FCSTD DOCUMENT  (FreeCAD 0.19R18750 (Git))
Label: #110-000 Assembly3
License: All rights reserved
LicenseURL: http://en.wikipedia.org/wiki/All_rights_reserved
objects: App::Link×90, Part::Feature×15, App::LinkGroup×1
note: 15 computed .brp shape members not serialized (recipe doc carries the construction recipe); baked Part::Feature solids carry a one-line shape summary decoded from their .brp

FEATURE [Part::Feature] Solid  label="XR5_R_CC25_P10.16_H_5DD3C33E"
  Placement = pos=(35.2425,24.765,0) rot=(0,0,1;1.5708rad)
  shape: bbox 2.5 x 10.96 x 5.1 mm, 11 faces (baked)
FEATURE [App::Link] Link  label="XR5_R_CC25_P10.16_H_5DD3C33E001"
  LinkPlacement = pos=(10.4775,-2.54,0) rot=(0,0,1;1.5708rad)
  LinkedObject = -> Solid
  Placement = pos=(10.4775,-2.54,0) rot=(0,0,1;1.5708rad)
FEATURE [Part::Feature] Solid001  label="RV55_Alpha_RV16AF-41-15R-XXX_5DD3C757"
  Placement = pos=(0,58.42,0) rot=(0,0,1;1.5708rad)
  shape: bbox 24.75 x 17.02 x 30.75 mm, 459 faces (baked)
FEATURE [App::Link] Link001  label="RV55_Alpha_RV16AF-41-15R-XXX_5DD3C758"
  LinkPlacement = pos=(-43.4975,58.42,0) rot=(0,0,1;1.5708rad)
  LinkedObject = -> Solid001
  Placement = pos=(-43.4975,58.42,0) rot=(0,0,1;1.5708rad)
FEATURE [Part::Feature] Solid002  label="JP20_R_0R_Wire_Jumper_P10.16_5DC277DA"
  Placement = pos=(13.6525,15.24,0) rot=(0,0,1;3.14159rad)
  shape: bbox 10.88 x 0.55 x 3.709 mm, 7 faces (baked)
FEATURE [App::Link] Link002  label="JP20_R_0R_Wire_Jumper_P10.16_5DC277DA001"
  LinkPlacement = pos=(13.6525,22.86,0) rot=(0,0,1;0rad)
  LinkedObject = -> Solid002
  Placement = pos=(13.6525,22.86,0) rot=(0,0,1;0rad)
FEATURE [App::Link] Link003  label="JP20_R_0R_Wire_Jumper_P10.16_5DC277DA002"
  LinkPlacement = pos=(10.4775,82.55,0) rot=(0,0,1;0rad)
  LinkedObject = -> Solid002
  Placement = pos=(10.4775,82.55,0) rot=(0,0,1;0rad)
FEATURE [App::Link] Link004  label="JP20_R_0R_Wire_Jumper_P10.16_5DC277DA003"
  LinkPlacement = pos=(26.9875,19.05,0) rot=(0,0,1;1.5708rad)
  LinkedObject = -> Solid002
  Placement = pos=(26.9875,19.05,0) rot=(0,0,1;1.5708rad)
FEATURE [App::Link] Link005  label="JP20_R_0R_Wire_Jumper_P10.16_5DC277DA004"
  LinkPlacement = pos=(27.6225,50.165,0) rot=(0,0,1;3.14159rad)
  LinkedObject = -> Solid002
  Placement = pos=(27.6225,50.165,0) rot=(0,0,1;3.14159rad)
FEATURE [App::Link] Link006  label="JP20_R_0R_Wire_Jumper_P10.16_5DC277DA005"
  LinkPlacement = pos=(13.0175,50.165,0) rot=(0,0,1;3.14159rad)
  LinkedObject = -> Solid002
  Placement = pos=(13.0175,50.165,0) rot=(0,0,1;3.14159rad)
FEATURE [App::Link] Link007  label="JP20_R_0R_Wire_Jumper_P10.16_5DC277DA006"
  LinkPlacement = pos=(30.1625,29.21,0) rot=(0,0,1;1.5708rad)
  LinkedObject = -> Solid002
  Placement = pos=(30.1625,29.21,0) rot=(0,0,1;1.5708rad)
FEATURE [App::Link] Link008  label="JP20_R_0R_Wire_Jumper_P10.16_5DC277DA007"
  LinkPlacement = pos=(13.6525,19.05,0) rot=(0,0,1;3.14159rad)
  LinkedObject = -> Solid002
  Placement = pos=(13.6525,19.05,0) rot=(0,0,1;3.14159rad)
FEATURE [App::Link] Link009  label="JP20_R_0R_Wire_Jumper_P10.16_5DC277DA008"
  LinkPlacement = pos=(-2.2225,12.065,0) rot=(0,0,-1;1.5708rad)
  LinkedObject = -> Solid002
  Placement = pos=(-2.2225,12.065,0) rot=(0,0,-1;1.5708rad)
FEATURE [App::Link] Link010  label="JP20_R_0R_Wire_Jumper_P10.16_5DC277DA009"
  LinkPlacement = pos=(-14.2875,31.75,0) rot=(0,0,1;3.14159rad)
  LinkedObject = -> Solid002
  Placement = pos=(-14.2875,31.75,0) rot=(0,0,1;3.14159rad)
FEATURE [App::Link] Link011  label="JP20_R_0R_Wire_Jumper_P10.16_5DC277DA010"
  LinkPlacement = pos=(-24.4475,10.16,0) rot=(0,0,1;1.5708rad)
  LinkedObject = -> Solid002
  Placement = pos=(-24.4475,10.16,0) rot=(0,0,1;1.5708rad)
FEATURE [App::Link] Link012  label="JP20_R_0R_Wire_Jumper_P10.16_5DC277DA011"
  LinkPlacement = pos=(-34.6075,21.59,0) rot=(0,0,1;1.5708rad)
  LinkedObject = -> Solid002
  Placement = pos=(-34.6075,21.59,0) rot=(0,0,1;1.5708rad)
FEATURE [App::Link] Link013  label="JP20_R_0R_Wire_Jumper_P10.16_5DC277DA012"
  LinkPlacement = pos=(26.9875,66.675,0) rot=(0,0,1;0rad)
  LinkedObject = -> Solid002
  Placement = pos=(26.9875,66.675,0) rot=(0,0,1;0rad)
FEATURE [App::Link] Link014  label="JP20_R_0R_Wire_Jumper_P10.16_5DC277DA013"
  LinkPlacement = pos=(-11.7475,67.31,0) rot=(0,0,1;0rad)
  LinkedObject = -> Solid002
  Placement = pos=(-11.7475,67.31,0) rot=(0,0,1;0rad)
FEATURE [App::Link] Link015  label="JP20_R_0R_Wire_Jumper_P10.16_5DC277DA014"
  LinkPlacement = pos=(-17.4625,81.915,0) rot=(0,0,1;0rad)
  LinkedObject = -> Solid002
  Placement = pos=(-17.4625,81.915,0) rot=(0,0,1;0rad)
FEATURE [Part::Feature] Solid003  label="XC7_Nichicon_UMA_Straight_D8_H5_P2.5_d0.45_LL2.6_5DC00BE9"
  Placement = pos=(11.7475,7.62,0) rot=(0,0,1;1.5708rad)
  shape: bbox 8.659 x 8.659 x 7.61 mm, 57 faces (baked)
FEATURE [Part::Feature] Solid004  label="RV52_User_Library_3362P_2_sp_5D8A0BC8"
  Placement = pos=(18.0975,74.93,0) rot=(0,0,1;0rad)
  shape: bbox 6.706 x 7.036 x 10.16 mm, 550 faces (baked)
FEATURE [Part::Feature] Solid005  label="XC8_FKS2G021001C00KSSD_5DC00BFC"
  Placement = pos=(2.2225,-2.5,0) rot=(0,0,-1;1.5708rad)
  shape: bbox 4.65 x 15.3 x 10.5 mm, 403 faces (baked)
FEATURE [Part::Feature] Solid006  label="XC6_Capacitor_Electrolytic_THT_Radial_Angled_D10_H17_P5_d0.6_h1.5_LL2.6_5DC00BE2"
  Placement = pos=(21.9075,-8.89,0) rot=(0,0,1;0rad)
  shape: bbox 10.82 x 18.92 x 13.01 mm, 66 faces (baked)
FEATURE [Part::Feature] Solid007  label="XC12_Nichicon_UMA_Straight_D8_H5_P2.5_d0.45_LL2.6_5DCF4B87"
  Placement = pos=(48.5775,22.86,0) rot=(0,0,-1;1.5708rad)
  shape: bbox 8.659 x 8.659 x 7.61 mm, 57 faces (baked)
FEATURE [Part::Feature] Solid008  label="XC10_Nichicon_UMA_Straight_D5_H5_P2_d0.45_LL2.6_5DC00C0A"
  Placement = pos=(44.1325,1.905,0) rot=(0,0,1;0rad)
  shape: bbox 5.412 x 5.412 x 7.61 mm, 57 faces (baked)
FEATURE [App::Link] Link016  label="XC10_Nichicon_UMA_Straight_D5_H5_P2_d0.45_LL2.6_5DC00C0A001"
  LinkPlacement = pos=(39.6875,-1.905,0) rot=(0,0,1;0rad)
  LinkedObject = -> Solid008
  Placement = pos=(39.6875,-1.905,0) rot=(0,0,1;0rad)
FEATURE [App::Link] Link017  label="XC12_Nichicon_UMA_Straight_D8_H5_P2.5_d0.45_LL2.6_5DCF4B088"
  LinkPlacement = pos=(44.7675,-6.985,0) rot=(0,0,1;0rad)
  LinkedObject = -> Solid007
  Placement = pos=(44.7675,-6.985,0) rot=(0,0,1;0rad)
FEATURE [App::Link] Link018  label="XC10_Nichicon_UMA_Straight_D5_H5_P2_d0.45_LL2.6_5DC00C0A002"
  LinkPlacement = pos=(-46.6725,5.715,0) rot=(0,0,-1;1.5708rad)
  LinkedObject = -> Solid008
  Placement = pos=(-46.6725,5.715,0) rot=(0,0,-1;1.5708rad)
FEATURE [Part::Feature] Solid009  label="XD6_DO-41_P10.16_5DC00C72"
  Placement = pos=(13.0175,-2.54,0) rot=(0,0,1;1.5708rad)
  shape: bbox 2.395 x 11.21 x 4.985 mm, 15 faces (baked)
FEATURE [App::Link] Link019  label="XD6_DO-41_P10.16_5DC00C073"
  LinkPlacement = pos=(-39.6875,-2.54,0) rot=(0,0,1;1.5708rad)
  LinkedObject = -> Solid009
  Placement = pos=(-39.6875,-2.54,0) rot=(0,0,1;1.5708rad)
FEATURE [App::Link] Link020  label="XD6_DO-41_P10.16_5DC00C074"
  LinkPlacement = pos=(42.2275,72.39,0) rot=(0,0,1;1.5708rad)
  LinkedObject = -> Solid009
  Placement = pos=(42.2275,72.39,0) rot=(0,0,1;1.5708rad)
FEATURE [App::Link] Link021  label="XR5_R_CC25_P10.16_H_5DD3C33E002"
  LinkPlacement = pos=(32.7025,29.21,0) rot=(0,0,1;1.5708rad)
  LinkedObject = -> Solid
  Placement = pos=(32.7025,29.21,0) rot=(0,0,1;1.5708rad)
FEATURE [App::Link] Link022  label="XR5_R_CC25_P10.16_H_5DD3C33E003"
  LinkPlacement = pos=(15.5575,-2.54,0) rot=(0,0,1;1.5708rad)
  LinkedObject = -> Solid
  Placement = pos=(15.5575,-2.54,0) rot=(0,0,1;1.5708rad)
FEATURE [App::Link] Link023  label="XR5_R_CC25_P10.16_H_5DD3C33E004"
  LinkPlacement = pos=(-42.2275,-2.54,0) rot=(0,0,-1;1.5708rad)
  LinkedObject = -> Solid
  Placement = pos=(-42.2275,-2.54,0) rot=(0,0,-1;1.5708rad)
FEATURE [App::Link] Link024  label="XR5_R_CC25_P10.16_H_5DD3C33E005"
  LinkPlacement = pos=(-51.1175,40.64,0) rot=(0,0,1;1.5708rad)
  LinkedObject = -> Solid
  Placement = pos=(-51.1175,40.64,0) rot=(0,0,1;1.5708rad)
FEATURE [App::Link] Link025  label="XR5_R_CC25_P10.16_H_5DD3C33E006"
  LinkPlacement = pos=(50.4825,74.93,0) rot=(0,0,1;1.5708rad)
  LinkedObject = -> Solid
  Placement = pos=(50.4825,74.93,0) rot=(0,0,1;1.5708rad)
FEATURE [App::Link] Link026  label="XR5_R_CC25_P10.16_H_5DD3C33E007"
  LinkPlacement = pos=(44.7675,78.74,0) rot=(0,0,-1;1.5708rad)
  LinkedObject = -> Solid
  Placement = pos=(44.7675,78.74,0) rot=(0,0,-1;1.5708rad)
FEATURE [App::Link] Link027  label="XR5_R_CC25_P10.16_H_5DD3C33E008"
  LinkPlacement = pos=(-20.6375,-2.54,0) rot=(0,0,-1;1.5708rad)
  LinkedObject = -> Solid
  Placement = pos=(-20.6375,-2.54,0) rot=(0,0,-1;1.5708rad)
FEATURE [App::Link] Link028  label="XR5_R_CC25_P10.16_H_5DD3C33E009"
  LinkPlacement = pos=(-37.1475,-2.54,0) rot=(0,0,-1;1.5708rad)
  LinkedObject = -> Solid
  Placement = pos=(-37.1475,-2.54,0) rot=(0,0,-1;1.5708rad)
FEATURE [App::Link] Link029  label="XR5_R_CC25_P10.16_H_5DD3C33E010"
  LinkPlacement = pos=(-23.1775,-2.54,0) rot=(0,0,-1;1.5708rad)
  LinkedObject = -> Solid
  Placement = pos=(-23.1775,-2.54,0) rot=(0,0,-1;1.5708rad)
FEATURE [App::Link] Link030  label="XR5_R_CC25_P10.16_H_5DD3C33E011"
  LinkPlacement = pos=(-34.6075,-2.54,0) rot=(0,0,-1;1.5708rad)
  LinkedObject = -> Solid
  Placement = pos=(-34.6075,-2.54,0) rot=(0,0,-1;1.5708rad)
FEATURE [App::Link] Link031  label="XR5_R_CC25_P10.16_H_5DD3C33E012"
  LinkPlacement = pos=(-29.5275,-2.54,0) rot=(0,0,-1;1.5708rad)
  LinkedObject = -> Solid
  Placement = pos=(-29.5275,-2.54,0) rot=(0,0,-1;1.5708rad)
FEATURE [App::Link] Link032  label="XR5_R_CC25_P10.16_H_5DD3C33E013"
  LinkPlacement = pos=(-7.9375,-2.54,0) rot=(0,0,-1;1.5708rad)
  LinkedObject = -> Solid
  Placement = pos=(-7.9375,-2.54,0) rot=(0,0,-1;1.5708rad)
FEATURE [App::Link] Link033  label="XR5_R_CC25_P10.16_H_5DD3C33E014"
  LinkPlacement = pos=(-5.3975,-2.54,0) rot=(0,0,-1;1.5708rad)
  LinkedObject = -> Solid
  Placement = pos=(-5.3975,-2.54,0) rot=(0,0,-1;1.5708rad)
FEATURE [App::Link] Link034  label="XR5_R_CC25_P10.16_H_5DD3C33E015"
  LinkPlacement = pos=(18.7325,58.42,0) rot=(0,0,-1;1.5708rad)
  LinkedObject = -> Solid
  Placement = pos=(18.7325,58.42,0) rot=(0,0,-1;1.5708rad)
FEATURE [App::Link] Link035  label="XR5_R_CC25_P10.16_H_5DD3C33E016"
  LinkPlacement = pos=(23.8125,58.42,0) rot=(0,0,-1;1.5708rad)
  LinkedObject = -> Solid
  Placement = pos=(23.8125,58.42,0) rot=(0,0,-1;1.5708rad)
FEATURE [App::Link] Link036  label="XR5_R_CC25_P10.16_H_5DD3C33E017"
  LinkPlacement = pos=(21.2725,58.42,0) rot=(0,0,-1;1.5708rad)
  LinkedObject = -> Solid
  Placement = pos=(21.2725,58.42,0) rot=(0,0,-1;1.5708rad)
FEATURE [App::Link] Link037  label="XR5_R_CC25_P10.16_H_5DD3C33E018"
  LinkPlacement = pos=(29.5275,74.93,0) rot=(0,0,1;1.5708rad)
  LinkedObject = -> Solid
  Placement = pos=(29.5275,74.93,0) rot=(0,0,1;1.5708rad)
FEATURE [App::Link] Link038  label="XR5_R_CC25_P10.16_H_5DD3C33E019"
  LinkPlacement = pos=(26.9875,74.93,0) rot=(0,0,-1;1.5708rad)
  LinkedObject = -> Solid
  Placement = pos=(26.9875,74.93,0) rot=(0,0,-1;1.5708rad)
FEATURE [App::Link] Link039  label="XR5_R_CC25_P10.16_H_5DD3C33E020"
  LinkPlacement = pos=(-44.7675,-2.54,0) rot=(0,0,-1;1.5708rad)
  LinkedObject = -> Solid
  Placement = pos=(-44.7675,-2.54,0) rot=(0,0,-1;1.5708rad)
FEATURE [App::Link] Link040  label="XR5_R_CC25_P10.16_H_5DD3C33E021"
  LinkPlacement = pos=(-37.7825,10.16,0) rot=(0,0,1;1.5708rad)
  LinkedObject = -> Solid
  Placement = pos=(-37.7825,10.16,0) rot=(0,0,1;1.5708rad)
FEATURE [App::Link] Link041  label="XR5_R_CC25_P10.16_H_5DD3C33E022"
  LinkPlacement = pos=(-47.9425,24.13,0) rot=(0,0,-1;1.5708rad)
  LinkedObject = -> Solid
  Placement = pos=(-47.9425,24.13,0) rot=(0,0,-1;1.5708rad)
FEATURE [App::Link] Link042  label="XR5_R_CC25_P10.16_H_5DD3C33E023"
  LinkPlacement = pos=(-50.4825,24.13,0) rot=(0,0,1;1.5708rad)
  LinkedObject = -> Solid
  Placement = pos=(-50.4825,24.13,0) rot=(0,0,1;1.5708rad)
FEATURE [App::Link] Link043  label="XR5_R_CC25_P10.16_H_5DD3C33E024"
  LinkPlacement = pos=(-44.1325,24.13,0) rot=(0,0,1;1.5708rad)
  LinkedObject = -> Solid
  Placement = pos=(-44.1325,24.13,0) rot=(0,0,1;1.5708rad)
FEATURE [App::Link] Link044  label="XR5_R_CC25_P10.16_H_5DD3C33E025"
  LinkPlacement = pos=(-40.3225,24.13,0) rot=(0,0,1;1.5708rad)
  LinkedObject = -> Solid
  Placement = pos=(-40.3225,24.13,0) rot=(0,0,1;1.5708rad)
FEATURE [App::Link] Link045  label="XR5_R_CC25_P10.16_H_5DD3C33E026"
  LinkPlacement = pos=(18.0975,40.64,0) rot=(0,0,-1;1.5708rad)
  LinkedObject = -> Solid
  Placement = pos=(18.0975,40.64,0) rot=(0,0,-1;1.5708rad)
FEATURE [App::Link] Link046  label="XR5_R_CC25_P10.16_H_5DD3C33E027"
  LinkPlacement = pos=(5.3975,74.93,0) rot=(0,0,1;1.5708rad)
  LinkedObject = -> Solid
  Placement = pos=(5.3975,74.93,0) rot=(0,0,1;1.5708rad)
FEATURE [App::Link] Link047  label="XR5_R_CC25_P10.16_H_5DD3C33E028"
  LinkPlacement = pos=(2.8575,74.93,0) rot=(0,0,-1;1.5708rad)
  LinkedObject = -> Solid
  Placement = pos=(2.8575,74.93,0) rot=(0,0,-1;1.5708rad)
FEATURE [App::Link] Link048  label="XR5_R_CC25_P10.16_H_5DD3C33E029"
  LinkPlacement = pos=(15.5575,40.64,0) rot=(0,0,-1;1.5708rad)
  LinkedObject = -> Solid
  Placement = pos=(15.5575,40.64,0) rot=(0,0,-1;1.5708rad)
FEATURE [App::Link] Link049  label="XR5_R_CC25_P10.16_H_5DD3C33E030"
  LinkPlacement = pos=(-0.9525,74.93,0) rot=(0,0,-1;1.5708rad)
  LinkedObject = -> Solid
  Placement = pos=(-0.9525,74.93,0) rot=(0,0,-1;1.5708rad)
FEATURE [App::Link] Link050  label="XR5_R_CC25_P10.16_H_5DD3C33E031"
  LinkPlacement = pos=(8.5725,40.64,0) rot=(0,0,-1;1.5708rad)
  LinkedObject = -> Solid
  Placement = pos=(8.5725,40.64,0) rot=(0,0,-1;1.5708rad)
FEATURE [App::Link] Link051  label="XR5_R_CC25_P10.16_H_5DD3C33E032"
  LinkPlacement = pos=(6.0325,40.64,0) rot=(0,0,1;1.5708rad)
  LinkedObject = -> Solid
  Placement = pos=(6.0325,40.64,0) rot=(0,0,1;1.5708rad)
FEATURE [App::Link] Link052  label="XR5_R_CC25_P10.16_H_5DD3C33E033"
  LinkPlacement = pos=(-1.5875,40.64,0) rot=(0,0,-1;1.5708rad)
  LinkedObject = -> Solid
  Placement = pos=(-1.5875,40.64,0) rot=(0,0,-1;1.5708rad)
FEATURE [App::Link] Link053  label="XR5_R_CC25_P10.16_H_5DD3C33E034"
  LinkPlacement = pos=(-5.3975,40.64,0) rot=(0,0,-1;1.5708rad)
  LinkedObject = -> Solid
  Placement = pos=(-5.3975,40.64,0) rot=(0,0,-1;1.5708rad)
FEATURE [App::Link] Link054  label="XR5_R_CC25_P10.16_H_5DD3C33E035"
  LinkPlacement = pos=(-11.7475,40.64,0) rot=(0,0,1;1.5708rad)
  LinkedObject = -> Solid
  Placement = pos=(-11.7475,40.64,0) rot=(0,0,1;1.5708rad)
FEATURE [App::Link] Link055  label="XR5_R_CC25_P10.16_H_5DD3C33E036"
  LinkPlacement = pos=(-9.2075,40.64,0) rot=(0,0,-1;1.5708rad)
  LinkedObject = -> Solid
  Placement = pos=(-9.2075,40.64,0) rot=(0,0,-1;1.5708rad)
FEATURE [App::Link] Link056  label="XR5_R_CC25_P10.16_H_5DD3C33E037"
  LinkPlacement = pos=(-19.3675,40.64,0) rot=(0,0,-1;1.5708rad)
  LinkedObject = -> Solid
  Placement = pos=(-19.3675,40.64,0) rot=(0,0,-1;1.5708rad)
FEATURE [App::Link] Link057  label="XR5_R_CC25_P10.16_H_5DD3C33E038"
  LinkPlacement = pos=(-21.9075,40.64,0) rot=(0,0,1;1.5708rad)
  LinkedObject = -> Solid
  Placement = pos=(-21.9075,40.64,0) rot=(0,0,1;1.5708rad)
FEATURE [App::Link] Link058  label="XR5_R_CC25_P10.16_H_5DD3C33E039"
  LinkPlacement = pos=(-28.8925,40.64,0) rot=(0,0,-1;1.5708rad)
  LinkedObject = -> Solid
  Placement = pos=(-28.8925,40.64,0) rot=(0,0,-1;1.5708rad)
FEATURE [App::Link] Link059  label="XR5_R_CC25_P10.16_H_5DD3C33E040"
  LinkPlacement = pos=(-33.3375,40.64,0) rot=(0,0,-1;1.5708rad)
  LinkedObject = -> Solid
  Placement = pos=(-33.3375,40.64,0) rot=(0,0,-1;1.5708rad)
FEATURE [App::Link] Link060  label="XR5_R_CC25_P10.16_H_5DD3C33E041"
  LinkPlacement = pos=(-46.6725,40.64,0) rot=(0,0,1;1.5708rad)
  LinkedObject = -> Solid
  Placement = pos=(-46.6725,40.64,0) rot=(0,0,1;1.5708rad)
FEATURE [App::Link] Link061  label="XR5_R_CC25_P10.16_H_5DD3C33E042"
  LinkPlacement = pos=(-37.1475,40.64,0) rot=(0,0,-1;1.5708rad)
  LinkedObject = -> Solid
  Placement = pos=(-37.1475,40.64,0) rot=(0,0,-1;1.5708rad)
FEATURE [App::Link] Link062  label="XR5_R_CC25_P10.16_H_5DD3C33E043"
  LinkPlacement = pos=(-40.3225,40.64,0) rot=(0,0,1;1.5708rad)
  LinkedObject = -> Solid
  Placement = pos=(-40.3225,40.64,0) rot=(0,0,1;1.5708rad)
FEATURE [App::Link] Link063  label="XR5_R_CC25_P10.16_H_5DD3C33E044"
  LinkPlacement = pos=(-23.8125,62.23,0) rot=(0,0,1;1.5708rad)
  LinkedObject = -> Solid
  Placement = pos=(-23.8125,62.23,0) rot=(0,0,1;1.5708rad)
FEATURE [App::Link] Link064  label="XR5_R_CC25_P10.16_H_5DD3C33E045"
  LinkPlacement = pos=(-21.2725,60.325,0) rot=(0,0,-1;1.5708rad)
  LinkedObject = -> Solid
  Placement = pos=(-21.2725,60.325,0) rot=(0,0,-1;1.5708rad)
FEATURE [App::Link] Link065  label="XR5_R_CC25_P10.16_H_5DD3C33E046"
  LinkPlacement = pos=(-30.1625,74.93,0) rot=(0,0,-1;1.5708rad)
  LinkedObject = -> Solid
  Placement = pos=(-30.1625,74.93,0) rot=(0,0,-1;1.5708rad)
FEATURE [App::Link] Link066  label="XR5_R_CC25_P10.16_H_5DD3C33E047"
  LinkPlacement = pos=(-32.7025,74.93,0) rot=(0,0,-1;1.5708rad)
  LinkedObject = -> Solid
  Placement = pos=(-32.7025,74.93,0) rot=(0,0,-1;1.5708rad)
FEATURE [App::Link] Link067  label="XR5_R_CC25_P10.16_H_5DD3C33E048"
  LinkPlacement = pos=(-35.2425,74.93,0) rot=(0,0,-1;1.5708rad)
  LinkedObject = -> Solid
  Placement = pos=(-35.2425,74.93,0) rot=(0,0,-1;1.5708rad)
FEATURE [App::Link] Link068  label="XR5_R_CC25_P10.16_H_5DD3C33E049"
  LinkPlacement = pos=(-45.4025,74.93,0) rot=(0,0,1;1.5708rad)
  LinkedObject = -> Solid
  Placement = pos=(-45.4025,74.93,0) rot=(0,0,1;1.5708rad)
FEATURE [App::Link] Link069  label="XR5_R_CC25_P10.16_H_5DD3C33E050"
  LinkPlacement = pos=(-47.9425,74.93,0) rot=(0,0,-1;1.5708rad)
  LinkedObject = -> Solid
  Placement = pos=(-47.9425,74.93,0) rot=(0,0,-1;1.5708rad)
FEATURE [Part::Feature] Solid010  label="XQ2_2N3904TAR_5DC00CE5"
  Placement = pos=(6.6675,-2.54,0) rot=(0,0,-1;1.5708rad)
  shape: bbox 3.625 x 5.54 x 10.42 mm, 233 faces (baked)
FEATURE [App::Link] Link070  label="XD6_DO-41_P10.16_5DC00C075"
  LinkPlacement = pos=(40.3225,24.765,0) rot=(0,0,1;1.5708rad)
  LinkedObject = -> Solid009
  Placement = pos=(40.3225,24.765,0) rot=(0,0,1;1.5708rad)
FEATURE [App::Link] Link071  label="XD6_DO-41_P10.16_5DC00C076"
  LinkPlacement = pos=(37.7825,24.765,0) rot=(0,0,-1;1.5708rad)
  LinkedObject = -> Solid009
  Placement = pos=(37.7825,24.765,0) rot=(0,0,-1;1.5708rad)
FEATURE [App::Link] Link072  label="XD6_DO-41_P10.16_5DC00C077"
  LinkPlacement = pos=(44.1325,17.145,0) rot=(0,0,1;0rad)
  LinkedObject = -> Solid009
  Placement = pos=(44.1325,17.145,0) rot=(0,0,1;0rad)
FEATURE [App::Link] Link073  label="XD6_DO-41_P10.16_5DC00C078"
  LinkPlacement = pos=(40.3225,34.29,0) rot=(0,0,1;3.14159rad)
  LinkedObject = -> Solid009
  Placement = pos=(40.3225,34.29,0) rot=(0,0,1;3.14159rad)
FEATURE [App::Link] Link074  label="XD6_DO-41_P10.16_5DC00C079"
  LinkPlacement = pos=(40.3225,31.75,0) rot=(0,0,1;0rad)
  LinkedObject = -> Solid009
  Placement = pos=(40.3225,31.75,0) rot=(0,0,1;0rad)
FEATURE [App::Link] Link075  label="XD6_DO-41_P10.16_5DC00C080"
  LinkPlacement = pos=(30.7975,-3.81,0) rot=(0,0,-1;1.5708rad)
  LinkedObject = -> Solid009
  Placement = pos=(30.7975,-3.81,0) rot=(0,0,-1;1.5708rad)
FEATURE [App::Link] Link076  label="XD6_DO-41_P10.16_5DC00C081"
  LinkPlacement = pos=(33.3375,-3.81,0) rot=(0,0,1;1.5708rad)
  LinkedObject = -> Solid009
  Placement = pos=(33.3375,-3.81,0) rot=(0,0,1;1.5708rad)
FEATURE [App::Link] Link077  label="XD6_DO-41_P10.16_5DC00C082"
  LinkPlacement = pos=(35.8775,10.16,0) rot=(0,0,-1;1.5708rad)
  LinkedObject = -> Solid009
  Placement = pos=(35.8775,10.16,0) rot=(0,0,-1;1.5708rad)
FEATURE [App::Link] Link078  label="XD6_DO-41_P10.16_5DC00C083"
  LinkPlacement = pos=(35.8775,-3.81,0) rot=(0,0,-1;1.5708rad)
  LinkedObject = -> Solid009
  Placement = pos=(35.8775,-3.81,0) rot=(0,0,-1;1.5708rad)
FEATURE [Part::Feature] Solid011  label="XU1_RC4558P_5DC00D2F"
  Placement = pos=(35.8775,74.93,0) rot=(0,0,1;1.5708rad)
  shape: bbox 9.59 x 7.87 x 7.1 mm, 280 faces (baked)
FEATURE [App::Link] Link079  label="XU1_RC4558P_5DC00D2F001"
  LinkPlacement = pos=(-30.7975,10.16,0) rot=(0,0,1;1.5708rad)
  LinkedObject = -> Solid011
  Placement = pos=(-30.7975,10.16,0) rot=(0,0,1;1.5708rad)
FEATURE [App::Link] Link080  label="XU1_RC4558P_5DC00D2F002"
  LinkPlacement = pos=(-8.5725,74.93,0) rot=(0,0,1;1.5708rad)
  LinkedObject = -> Solid011
  Placement = pos=(-8.5725,74.93,0) rot=(0,0,1;1.5708rad)
FEATURE [App::Link] Link081  label="XU1_RC4558P_5DC00D2F003"
  LinkPlacement = pos=(0.9525,27.305,0) rot=(0,0,1;1.5708rad)
  LinkedObject = -> Solid011
  Placement = pos=(0.9525,27.305,0) rot=(0,0,1;1.5708rad)
FEATURE [App::Link] Link082  label="XU1_RC4558P_5DC00D2F004"
  LinkPlacement = pos=(-28.2575,29.21,0) rot=(0,0,1;1.5708rad)
  LinkedObject = -> Solid011
  Placement = pos=(-28.2575,29.21,0) rot=(0,0,1;1.5708rad)
FEATURE [App::Link] Link083  label="XU1_RC4558P_5DC00D2F005"
  LinkPlacement = pos=(-20.0025,74.93,0) rot=(0,0,1;1.5708rad)
  LinkedObject = -> Solid011
  Placement = pos=(-20.0025,74.93,0) rot=(0,0,1;1.5708rad)
FEATURE [App::Link] Link084  label="XQ2_2N3904TAR_5DC00CE006"
  LinkPlacement = pos=(-18.0975,6.985,0) rot=(0,0,1;3.14159rad)
  LinkedObject = -> Solid010
  Placement = pos=(-18.0975,6.985,0) rot=(0,0,1;3.14159rad)
FEATURE [Part::Feature] Solid012  label="C16_MKS2C034701C00KSSD_5D8A0691"
  Placement = pos=(12.3825,74.93,0) rot=(0,0,1;1.5708rad)
  shape: bbox 4.65 x 15.3 x 10.5 mm, 395 faces (baked)
FEATURE [Part::Feature] Solid013  label="C23_FKS2G016801B00KSSD_5DD3B7C2"
  Placement = pos=(8.5725,74.93,0) rot=(0,0,1;1.5708rad)
  shape: bbox 3.9 x 15.3 x 9.5 mm, 432 faces (baked)
FEATURE [App::Link] Link085  label="C23_FKS2G016801B00KSSD_5DD3B7C003"
  LinkPlacement = pos=(12.3825,40.64,0) rot=(0,0,1;1.5708rad)
  LinkedObject = -> Solid013
  Placement = pos=(12.3825,40.64,0) rot=(0,0,1;1.5708rad)
FEATURE [App::Link] Link086  label="C23_FKS2G016801B00KSSD_5DD3B7C004"
  LinkPlacement = pos=(2.2225,40.64,0) rot=(0,0,-1;1.5708rad)
  LinkedObject = -> Solid013
  Placement = pos=(2.2225,40.64,0) rot=(0,0,-1;1.5708rad)
FEATURE [App::Link] Link087  label="C23_FKS2G016801B00KSSD_5DD3B7C005"
  LinkPlacement = pos=(-15.5575,40.64,0) rot=(0,0,-1;1.5708rad)
  LinkedObject = -> Solid013
  Placement = pos=(-15.5575,40.64,0) rot=(0,0,-1;1.5708rad)
FEATURE [App::Link] Link088  label="C23_FKS2G016801B00KSSD_5DD3B7C006"
  LinkPlacement = pos=(-25.7175,40.64,0) rot=(0,0,-1;1.5708rad)
  LinkedObject = -> Solid013
  Placement = pos=(-25.7175,40.64,0) rot=(0,0,-1;1.5708rad)
FEATURE [App::Link] Link089  label="C23_FKS2G016801B00KSSD_5DD3B7C007"
  LinkPlacement = pos=(-43.4975,40.64,0) rot=(0,0,-1;1.5708rad)
  LinkedObject = -> Solid013
  Placement = pos=(-43.4975,40.64,0) rot=(0,0,-1;1.5708rad)
FEATURE [Part::Feature] Compound  label="Pcb_sp"
  shape: bbox 112.4 x 102.9 x 31.47 mm, 7037 faces, 48 solids (baked)
FEATURE [App::LinkGroup] LinkGroup  label="#110-000"
  ElementList = -> [Solid,Link,Solid001,Link001,Solid002,Link002,Link003,Link004,Link005,Link006,Link007,Link008,Link009,Link010,Link011,Link012,Link013,Link014,Link015,Solid003,Solid004,Solid005,Solid006,Solid007,Solid008,Link016,Link017,Link018,Solid009,Link019,Link020,Link021,Link022,Link023,Link024,Link025,Link026,Link027,Link028,Link029,Link030,Link031,Link032,Link033,Link034,Link035,Link036,Link037,Link038,+56 more]
  LinkMode = 0
